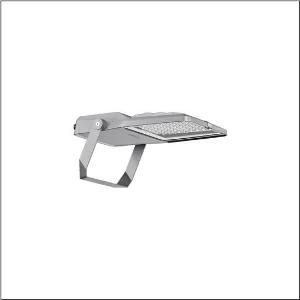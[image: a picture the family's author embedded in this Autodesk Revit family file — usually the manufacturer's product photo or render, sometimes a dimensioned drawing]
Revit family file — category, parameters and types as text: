
# Revit family: floodlight_fl_21_iq_mini___pl52_5xa7771b4d1a_5516
name_source: partatom
category: Lighting Fixtures
units: mm (PartAtom-declared; Revit-internal decimal feet)

## family parameters
Cut with Voids When Loaded = No
Host = Face
Light Source = No
Part Type = Normal
Room Calculation Point = No
Round Connector Dimension = Use Diameter
Shared = No

## types (1)
- --- (1 x LED, 6490 lm, 45.5 W, 4000K)
    Apparent Load = 46 VA
    CIE Flux Codes = 26 60 98 100 100
    Color Rendering = 70
    Color Temperature = 4000K
    Default Elevation = 1800 mm
    Description = Floodlight FL 21 iQ mini, floodlight, primary light control with lens, of PMMA, primary optical cover: protective disc, of toughened safety glass, transparent, light distribution: PL52, light emission: direct distribution, installation type: surface-mounted, LED, High Power LED, rated luminous flux: 6.490lm, luminous efficacy: 143lm/W, light colour: 740, colour temperature: 4000K, control: Auto-Match, Temp-Guard, Lumen-Switch, Night-Set, Smart-Wire, Light-Fading, Desk-Remote (wireless, voltage-free reading and setting of iQ features in the workshop via application-optimized NFC function/RFID function), optimised constant luminous flux control (CLO 2.0), with terminal, 6-pole, mains connection: 220..240V, AC, 50/60Hz, start of lifetime: 46W, end of service life: 48W, reduction: 22W, luminaire housing, of diecast aluminium, powder-coated, Siteco® metallic grey (DB 702S), corrosivity category C5 mid according to DIN EN ISO 12944, sealing non-destructively replaceable, mounting bracket, of steel, galvanised, powder-coated, Siteco® metallic grey (DB 702S), protection rating (complete): IP66, insulation class (complete): insulation class II (safety insulation), certification: CE, ENEC, VDE, protection symbol: D, impact resistance: IK08, permissible operating ambient temperature: -40..+40°C, permissible operating ambient temperature for outdoor applications: -40..+50°C, standard: DIN EN 12944, LABS conformity tested according to VDMA 24364:2018-05, packaging unit: 1 piece

Light Distribution: PL52
    Height = 70 mm
    Lamp = 1 x LED
    Lamp Light Flux = 6490 lm
    Lamp Power = 45.5 W
    Lamp count = 1
    Length = 485 mm
    Luminous efficacy = 143 lm/W
    Manufacturer = Siteco
    ModVariant = No
    Model = 5XA7771B4D1A
    Mounting Place = Wall
    Mounting Type = Surface mounted
    Number of Poles = 1
    OnlyDefault = Yes
    Power Factor = 1
    Product Name = Floodlight FL 21 iQ mini | PL52
    Product group = floodlight | wall mounted
    ProductGroupID = 2001
    Protection Class = Protection class II
    Protection Degree = IP 66
    RLX_Detail_Level = 1
    RLX_Emergency_Light_Flux = 0 lm
    RLX_Emergency_Type = 0
    RLX_Emergency_Type_DB = No
    RlxData = <blob elided: 96309 chars, md5=2da99e94>
    Socket = socket
    Standby Power = 0 W
    System Light Flux = 6490 lm
    System Power = 46 W
    Type Comments = factory setting: luminous flux: 100 % | dim-lin: 254 | 463 mA
    Type Image = l_1006845.jpg
    URL = http://relux.com
    VarID = @adj_115211
    Voltage = 0 V
    Weight = 0.00 kg
    Width = 337 mm

## geometry (parser evidence)
native form markers: Blend x4, Sweep x14
no freeform markers — native parametric forms only
